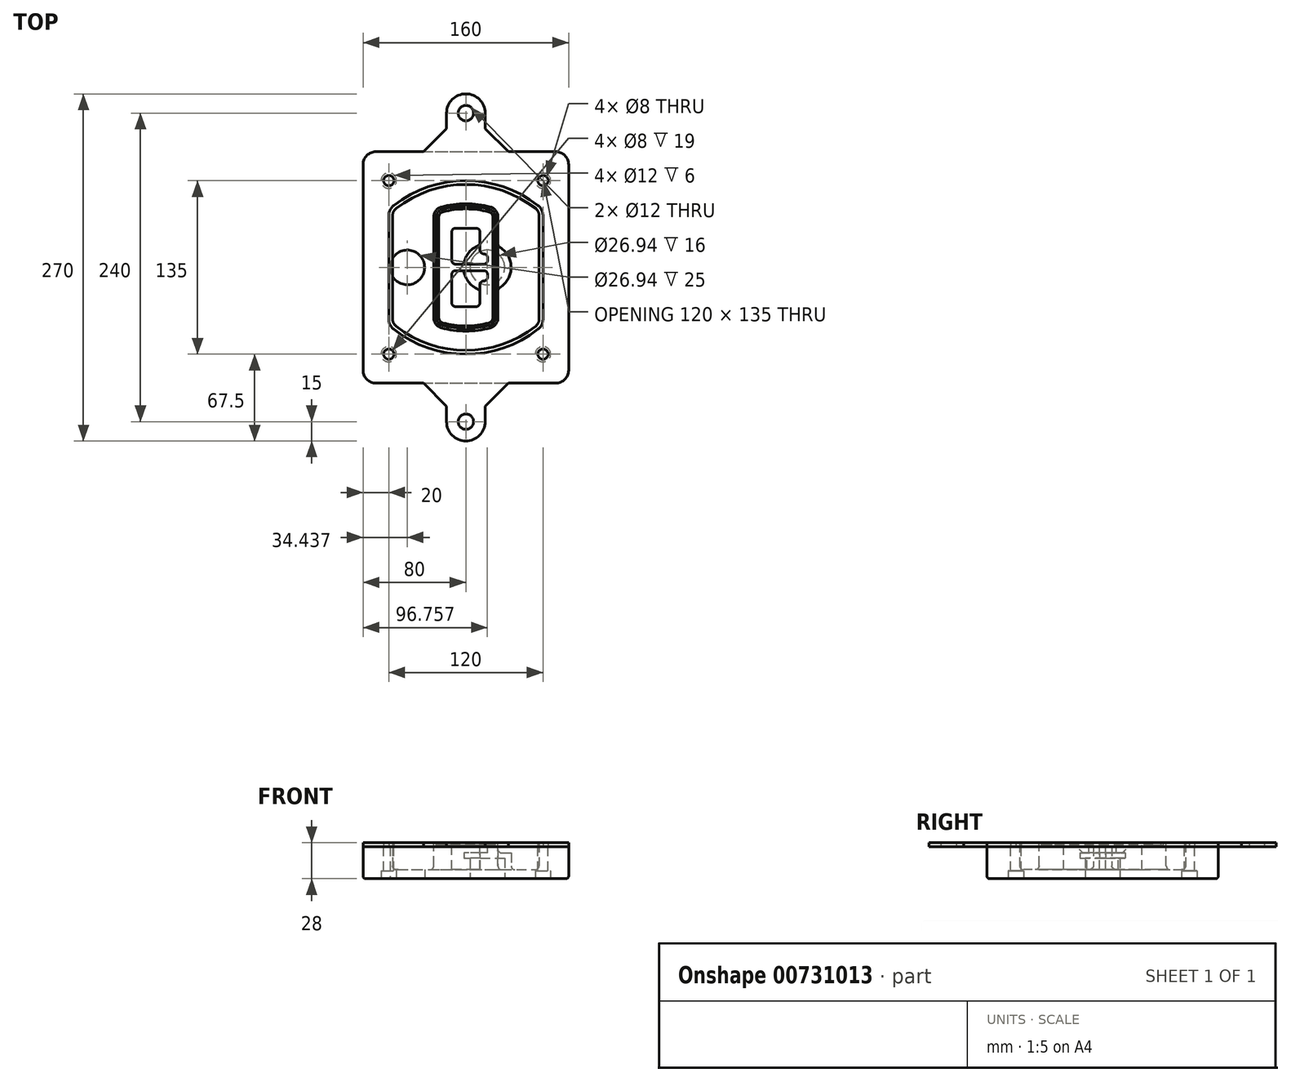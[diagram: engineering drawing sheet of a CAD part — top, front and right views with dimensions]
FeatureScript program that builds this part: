
annotation { "Feature Type Name" : "Feature", "Feature Type Description" : "" }
export const myFeature = defineFeature(function(context is Context, id is Id, definition is map)
    precondition{}
    {
        {
            var Q0;
            Q0=qCreatedBy(makeId("Top.planeOp"),FACE);
            var sketch = newSketch(context, id + "F0", { "sketchPlane" : qUnion([Q0])});
            skPoint(sketch, "E0.rect.middle", {"position": v(0, 0) * mm});
            skLineSegment(sketch, "E1.bottom", {"start": v(-70, -90) * mm, "end": v(70, -90) * mm});
            skLineSegment(sketch, "E1.top", {"start": v(-70, 90) * mm, "end": v(70, 90) * mm});
            skLineSegment(sketch, "E1.left", {"start": v(-80, -80) * mm, "end": v(-80, 80) * mm});
            skLineSegment(sketch, "E1.right", {"start": v(80, -80) * mm, "end": v(80, 80) * mm});
            skLineSegment(sketch, "E2", {"start": v(-80, 90) * mm, "end": v(80, -90) * mm, "construction": true});
            skLineSegment(sketch, "E3", {"start": v(80, 90) * mm, "end": v(-80, -90) * mm, "construction": true});
            skCircle(sketch, "E4", {"center": v(-60, 67.5) * mm, "radius": 4 * mm});
            skCircle(sketch, "E5", {"center": v(60, 67.5) * mm, "radius": 4 * mm});
            skCircle(sketch, "E6", {"center": v(60, -67.5) * mm, "radius": 4 * mm});
            skCircle(sketch, "E7", {"center": v(-60, -67.5) * mm, "radius": 4 * mm});
            skLineSegment(sketch, "E8", {"start": v(-60, 67.5) * mm, "end": v(60, 67.5) * mm, "construction": true});
            skLineSegment(sketch, "E9", {"start": v(60, 67.5) * mm, "end": v(60, -67.5) * mm, "construction": true});
            skLineSegment(sketch, "E10", {"start": v(60, -67.5) * mm, "end": v(-60, -67.5) * mm, "construction": true});
            skLineSegment(sketch, "E11", {"start": v(-60, -67.5) * mm, "end": v(-60, 67.5) * mm, "construction": true});
            skLineSegment(sketch, "E12", {"start": v(-60, 40.3) * mm, "end": v(-60, -40.3) * mm});
            skLineSegment(sketch, "E13", {"start": v(60, 40.3) * mm, "end": v(60, -40.3) * mm});
            skArc(sketch, "E14", {"start": v(56.15, 48.18) * mm, "mid": v(0, 67.5) * mm, "end": v(-56.15, 48.18) * mm});
            skArc(sketch, "E15", {"start": v(-56.15, -48.18) * mm, "mid": v(0, -67.5) * mm, "end": v(56.15, -48.18) * mm});
            skLineSegment(sketch, "E16", {"start": v(-60, 0) * mm, "end": v(60, 0) * mm, "construction": true});
            skPoint(sketch, "E17.visualSharp", {"position": v(-60, -45) * mm});
            skArc(sketch, "E17.filletArc", {"start": v(-60, -40.3) * mm, "mid": v(-58.99, -44.68) * mm, "end": v(-56.15, -48.18) * mm});
            skPoint(sketch, "E18.visualSharp", {"position": v(-60, 45) * mm});
            skArc(sketch, "E18.filletArc", {"start": v(-56.15, 48.18) * mm, "mid": v(-58.99, 44.68) * mm, "end": v(-60, 40.3) * mm});
            skPoint(sketch, "E19.visualSharp", {"position": v(60, 45) * mm});
            skArc(sketch, "E19.filletArc", {"start": v(60, 40.3) * mm, "mid": v(58.99, 44.68) * mm, "end": v(56.15, 48.18) * mm});
            skPoint(sketch, "E20.visualSharp", {"position": v(60, -45) * mm});
            skArc(sketch, "E20.filletArc", {"start": v(56.15, -48.18) * mm, "mid": v(58.99, -44.68) * mm, "end": v(60, -40.3) * mm});
            skPoint(sketch, "E21.visualSharp", {"position": v(-80, 90) * mm});
            skArc(sketch, "E21.filletArc", {"start": v(-70, 90) * mm, "mid": v(-77.07, 87.07) * mm, "end": v(-80, 80) * mm});
            skPoint(sketch, "E22.visualSharp", {"position": v(80, 90) * mm});
            skArc(sketch, "E22.filletArc", {"start": v(80, 80) * mm, "mid": v(77.07, 87.07) * mm, "end": v(70, 90) * mm});
            skPoint(sketch, "E23.visualSharp", {"position": v(80, -90) * mm});
            skArc(sketch, "E23.filletArc", {"start": v(70, -90) * mm, "mid": v(77.07, -87.07) * mm, "end": v(80, -80) * mm});
            skPoint(sketch, "E24.visualSharp", {"position": v(-80, -90) * mm});
            skArc(sketch, "E24.filletArc", {"start": v(-80, -80) * mm, "mid": v(-77.07, -87.07) * mm, "end": v(-70, -90) * mm});
            skArc(sketch, "E25.0", {"start": v(57, 40.3) * mm, "mid": v(56.3, 43.36) * mm, "end": v(54.3, 45.81) * mm});
            skLineSegment(sketch, "E25.1", {"start": v(57, 40.3) * mm, "end": v(57, -40.3) * mm});
            skArc(sketch, "E25.2", {"start": v(54.3, -45.81) * mm, "mid": v(56.3, -43.36) * mm, "end": v(57, -40.3) * mm});
            skArc(sketch, "E25.3", {"start": v(-54.3, -45.81) * mm, "mid": v(0, -64.5) * mm, "end": v(54.3, -45.81) * mm});
            skArc(sketch, "E25.4", {"start": v(-57, -40.3) * mm, "mid": v(-56.3, -43.36) * mm, "end": v(-54.3, -45.81) * mm});
            skArc(sketch, "E25.5", {"start": v(54.3, 45.81) * mm, "mid": v(0, 64.5) * mm, "end": v(-54.3, 45.81) * mm});
            skLineSegment(sketch, "E25.6", {"start": v(-57, 40.3) * mm, "end": v(-57, -40.3) * mm});
            skArc(sketch, "E25.7", {"start": v(-54.3, 45.81) * mm, "mid": v(-56.3, 43.36) * mm, "end": v(-57, 40.3) * mm});
            skArc(sketch, "E26.0", {"start": v(-58.62, 51.33) * mm, "mid": v(-62.58, 46.43) * mm, "end": v(-64, 40.3) * mm});
            skArc(sketch, "E26.1", {"start": v(58.62, 51.33) * mm, "mid": v(0, 71.5) * mm, "end": v(-58.62, 51.33) * mm});
            skArc(sketch, "E26.2", {"start": v(64, 40.3) * mm, "mid": v(62.58, 46.43) * mm, "end": v(58.62, 51.33) * mm});
            skLineSegment(sketch, "E26.3", {"start": v(64, 40.3) * mm, "end": v(64, -40.3) * mm});
            skArc(sketch, "E26.4", {"start": v(58.62, -51.33) * mm, "mid": v(62.58, -46.43) * mm, "end": v(64, -40.3) * mm});
            skLineSegment(sketch, "E26.5", {"start": v(-64, 40.3) * mm, "end": v(-64, -40.3) * mm});
            skArc(sketch, "E26.6", {"start": v(-58.62, -51.33) * mm, "mid": v(0, -71.5) * mm, "end": v(58.62, -51.33) * mm});
            skArc(sketch, "E26.7", {"start": v(-64, -40.3) * mm, "mid": v(-62.58, -46.43) * mm, "end": v(-58.62, -51.33) * mm});
            skSolve(sketch);
        }
        {
            var Q0;
            Q0=makeQuery(id+"F0.imprint","IMPRINT",FACE,{"disambiguationData":[TD([[makeQuery(id+"F0.imprint","IMPRINT",EDGE,{"derivedFrom":sQuery(id+"F0.wireOp",EDGE,"E1.bottom")}),1.0]])]});
            var Q1;
            Q1=makeQuery(id+"F0.imprint","IMPRINT",FACE,{"disambiguationData":[TD([[makeQuery(id+"F0.imprint","IMPRINT",EDGE,{"derivedFrom":sQuery(id+"F0.wireOp",EDGE,"E12")}),1.0]])]});
            var Q2;
            Q2=makeQuery(id+"F0.imprint","IMPRINT",FACE,{"disambiguationData":[TD([[makeQuery(id+"F0.imprint","IMPRINT",EDGE,{"derivedFrom":sQuery(id+"F0.wireOp",EDGE,"E25.0")}),1.0]])]});
            var Q3;
            Q3=makeQuery(id+"F0.imprint","IMPRINT",FACE,{"disambiguationData":[TD([[makeQuery(id+"F0.imprint","IMPRINT",EDGE,{"derivedFrom":sQuery(id+"F0.wireOp",EDGE,"E12")}),-1.0]])]});
            extrude(context, id + "F1", {"entities" : qUnion([Q0, Q1, Q2, Q3]), "oppositeDirection" : true, "depth" : 25 * mm, "offsetDistance" : 25 * mm});
        }
        {
            var Q0;
            Q0=makeQuery(id+"F0.imprint","IMPRINT",FACE,{"disambiguationData":[TD([[makeQuery(id+"F0.imprint","IMPRINT",EDGE,{"derivedFrom":sQuery(id+"F0.wireOp",EDGE,"E12")}),1.0]])]});
            extrude(context, id + "F2", {"entities" : qUnion([Q0]), "operationType" : NewBodyOperationType.ADD, "depth" : 3 * mm, "offsetDistance" : 25 * mm});
        }
        {
            var Q0;
            Q0=makeQuery(id+"F0.imprint","IMPRINT",FACE,{"disambiguationData":[TD([[makeQuery(id+"F0.imprint","IMPRINT",EDGE,{"derivedFrom":sQuery(id+"F0.wireOp",EDGE,"E25.0")}),1.0]])]});
            extrude(context, id + "F3", {"entities" : qUnion([Q0]), "operationType" : NewBodyOperationType.REMOVE, "oppositeDirection" : true, "depth" : 18 * mm, "offsetDistance" : 25 * mm});
        }
        {
            var Q0;
            Q0=makeQuery(id+"F2.opExtrude","CAP_FACE",FACE,{"disambiguationData":[OSD([sQuery(id+"F0.wireOp",EDGE,"E12"),sQuery(id+"F0.wireOp",EDGE,"E13"),sQuery(id+"F0.wireOp",EDGE,"E14"),sQuery(id+"F0.wireOp",EDGE,"E15"),sQuery(id+"F0.wireOp",EDGE,"E17.filletArc"),sQuery(id+"F0.wireOp",EDGE,"E18.filletArc"),sQuery(id+"F0.wireOp",EDGE,"E19.filletArc"),sQuery(id+"F0.wireOp",EDGE,"E20.filletArc"),sQuery(id+"F0.wireOp",EDGE,"E25.0"),sQuery(id+"F0.wireOp",EDGE,"E25.1"),sQuery(id+"F0.wireOp",EDGE,"E25.2"),sQuery(id+"F0.wireOp",EDGE,"E25.3"),sQuery(id+"F0.wireOp",EDGE,"E25.4"),sQuery(id+"F0.wireOp",EDGE,"E25.5"),sQuery(id+"F0.wireOp",EDGE,"E25.6"),sQuery(id+"F0.wireOp",EDGE,"E25.7")])],"isStart":false});
            var sketch = newSketch(context, id + "F4", { "sketchPlane" : qUnion([Q0])});
            skArc(sketch, "E27.0", {"start": v(-19.08, -46.97) * mm, "mid": v(0, -49.5) * mm, "end": v(19.08, -46.97) * mm});
            skArc(sketch, "E28.0", {"start": v(19.08, 46.97) * mm, "mid": v(0, 49.5) * mm, "end": v(-19.08, 46.97) * mm});
            skLineSegment(sketch, "E29", {"start": v(-25, 39.25) * mm, "end": v(-25, -39.25) * mm});
            skLineSegment(sketch, "E30", {"start": v(25, 39.25) * mm, "end": v(25, -39.25) * mm});
            skLineSegment(sketch, "E31", {"start": v(-25, 45.1) * mm, "end": v(25, 45.1) * mm, "construction": true});
            skLineSegment(sketch, "E32", {"start": v(-25, -45.1) * mm, "end": v(25, -45.1) * mm, "construction": true});
            skPoint(sketch, "E33.visualSharp", {"position": v(-25, 45.1) * mm});
            skArc(sketch, "E33.filletArc", {"start": v(-19.08, 46.97) * mm, "mid": v(-23.35, 44.11) * mm, "end": v(-25, 39.25) * mm});
            skPoint(sketch, "E34.visualSharp", {"position": v(25, 45.1) * mm});
            skArc(sketch, "E34.filletArc", {"start": v(25, 39.25) * mm, "mid": v(23.35, 44.11) * mm, "end": v(19.08, 46.97) * mm});
            skPoint(sketch, "E35.visualSharp", {"position": v(25, -45.1) * mm});
            skArc(sketch, "E35.filletArc", {"start": v(19.08, -46.97) * mm, "mid": v(23.35, -44.11) * mm, "end": v(25, -39.25) * mm});
            skPoint(sketch, "E36.visualSharp", {"position": v(-25, -45.1) * mm});
            skArc(sketch, "E36.filletArc", {"start": v(-25, -39.25) * mm, "mid": v(-23.35, -44.11) * mm, "end": v(-19.08, -46.97) * mm});
            skArc(sketch, "E37.0", {"start": v(54.3, 45.81) * mm, "mid": v(0, 64.5) * mm, "end": v(-54.3, 45.81) * mm});
            skArc(sketch, "E37.1", {"start": v(-54.3, 45.81) * mm, "mid": v(-56.3, 43.36) * mm, "end": v(-57, 40.3) * mm});
            skLineSegment(sketch, "E37.2", {"start": v(-57, 40.3) * mm, "end": v(-57, -40.3) * mm});
            skArc(sketch, "E37.3", {"start": v(-57, -40.3) * mm, "mid": v(-56.3, -43.36) * mm, "end": v(-54.3, -45.81) * mm});
            skArc(sketch, "E37.4", {"start": v(-54.3, -45.81) * mm, "mid": v(0, -64.5) * mm, "end": v(54.3, -45.81) * mm});
            skArc(sketch, "E37.5", {"start": v(54.3, -45.81) * mm, "mid": v(56.3, -43.36) * mm, "end": v(57, -40.3) * mm});
            skLineSegment(sketch, "E37.6", {"start": v(57, 40.3) * mm, "end": v(57, -40.3) * mm});
            skArc(sketch, "E37.7", {"start": v(57, 40.3) * mm, "mid": v(56.3, 43.36) * mm, "end": v(54.3, 45.81) * mm});
            skLineSegment(sketch, "E38.0", {"start": v(23, 39.25) * mm, "end": v(23, -39.25) * mm});
            skArc(sketch, "E38.1", {"start": v(18.56, -45.04) * mm, "mid": v(21.76, -42.9) * mm, "end": v(23, -39.25) * mm});
            skArc(sketch, "E38.2", {"start": v(-18.56, -45.04) * mm, "mid": v(0, -47.5) * mm, "end": v(18.56, -45.04) * mm});
            skArc(sketch, "E38.3", {"start": v(-23, -39.25) * mm, "mid": v(-21.76, -42.9) * mm, "end": v(-18.56, -45.04) * mm});
            skLineSegment(sketch, "E38.4", {"start": v(-23, 39.25) * mm, "end": v(-23, -39.25) * mm});
            skArc(sketch, "E38.5", {"start": v(23, 39.25) * mm, "mid": v(21.76, 42.9) * mm, "end": v(18.56, 45.04) * mm});
            skArc(sketch, "E38.6", {"start": v(-18.56, 45.04) * mm, "mid": v(-21.76, 42.9) * mm, "end": v(-23, 39.25) * mm});
            skArc(sketch, "E38.7", {"start": v(18.56, 45.04) * mm, "mid": v(0, 47.5) * mm, "end": v(-18.56, 45.04) * mm});
            skArc(sketch, "E39.0", {"start": v(21, 39.25) * mm, "mid": v(20.18, 41.68) * mm, "end": v(18.04, 43.1) * mm});
            skLineSegment(sketch, "E39.1", {"start": v(21, 39.25) * mm, "end": v(21, -39.25) * mm});
            skArc(sketch, "E39.2", {"start": v(18.04, -43.1) * mm, "mid": v(20.18, -41.68) * mm, "end": v(21, -39.25) * mm});
            skArc(sketch, "E39.3", {"start": v(-18.04, -43.1) * mm, "mid": v(0, -45.5) * mm, "end": v(18.04, -43.1) * mm});
            skArc(sketch, "E39.4", {"start": v(-21, -39.25) * mm, "mid": v(-20.18, -41.68) * mm, "end": v(-18.04, -43.1) * mm});
            skArc(sketch, "E39.5", {"start": v(18.04, 43.1) * mm, "mid": v(0, 45.5) * mm, "end": v(-18.04, 43.1) * mm});
            skLineSegment(sketch, "E39.6", {"start": v(-21, 39.25) * mm, "end": v(-21, -39.25) * mm});
            skArc(sketch, "E39.7", {"start": v(-18.04, 43.1) * mm, "mid": v(-20.18, 41.68) * mm, "end": v(-21, 39.25) * mm});
            skLineSegment(sketch, "E40", {"start": v(-25, 0) * mm, "end": v(25, 0) * mm, "construction": true});
            skLineSegment(sketch, "E41", {"start": v(-11, 5.5) * mm, "end": v(-11, 27.5) * mm});
            skLineSegment(sketch, "E42", {"start": v(-8, 30.5) * mm, "end": v(8, 30.5) * mm});
            skLineSegment(sketch, "E43", {"start": v(11, 27.5) * mm, "end": v(11, 13.5) * mm});
            skLineSegment(sketch, "E44", {"start": v(14, 10.5) * mm, "end": v(14, 10.5) * mm});
            skLineSegment(sketch, "E45", {"start": v(17, 7.5) * mm, "end": v(17, 5.5) * mm});
            skLineSegment(sketch, "E46", {"start": v(14, 2.5) * mm, "end": v(-8, 2.5) * mm});
            skPoint(sketch, "E47.visualSharp", {"position": v(-11, 30.5) * mm});
            skArc(sketch, "E47.filletArc", {"start": v(-8, 30.5) * mm, "mid": v(-10.12, 29.62) * mm, "end": v(-11, 27.5) * mm});
            skPoint(sketch, "E48.visualSharp", {"position": v(11, 30.5) * mm});
            skArc(sketch, "E48.filletArc", {"start": v(11, 27.5) * mm, "mid": v(10.12, 29.62) * mm, "end": v(8, 30.5) * mm});
            skPoint(sketch, "E49.visualSharp", {"position": v(11, 10.5) * mm});
            skArc(sketch, "E49.filletArc", {"start": v(11, 13.5) * mm, "mid": v(11.88, 11.38) * mm, "end": v(14, 10.5) * mm});
            skPoint(sketch, "E50.visualSharp", {"position": v(17, 10.5) * mm});
            skArc(sketch, "E50.filletArc", {"start": v(17, 7.5) * mm, "mid": v(16.12, 9.62) * mm, "end": v(14, 10.5) * mm});
            skPoint(sketch, "E51.visualSharp", {"position": v(17, 2.5) * mm});
            skArc(sketch, "E51.filletArc", {"start": v(14, 2.5) * mm, "mid": v(16.12, 3.38) * mm, "end": v(17, 5.5) * mm});
            skPoint(sketch, "E52.visualSharp", {"position": v(-11, 2.5) * mm});
            skArc(sketch, "E52.filletArc", {"start": v(-11, 5.5) * mm, "mid": v(-10.12, 3.38) * mm, "end": v(-8, 2.5) * mm});
            skLineSegment(sketch, "E53.0.MirrorCS", {"start": v(14, -2.5) * mm, "end": v(-8, -2.5) * mm});
            skArc(sketch, "E54.0.MirrorCS", {"start": v(-11, -5.5) * mm, "mid": v(-10.12, -3.38) * mm, "end": v(-8, -2.5) * mm});
            skLineSegment(sketch, "E55.0.MirrorCS", {"start": v(-11, -5.5) * mm, "end": v(-11, -27.5) * mm});
            skArc(sketch, "E56.0.MirrorCS", {"start": v(-8, -30.5) * mm, "mid": v(-10.12, -29.62) * mm, "end": v(-11, -27.5) * mm});
            skLineSegment(sketch, "E57.0.MirrorCS", {"start": v(-8, -30.5) * mm, "end": v(8, -30.5) * mm});
            skArc(sketch, "E58.0.MirrorCS", {"start": v(11, -27.5) * mm, "mid": v(10.12, -29.62) * mm, "end": v(8, -30.5) * mm});
            skLineSegment(sketch, "E59.0.MirrorCS", {"start": v(11, -27.5) * mm, "end": v(11, -13.5) * mm});
            skArc(sketch, "E60.0.MirrorCS", {"start": v(11, -13.5) * mm, "mid": v(11.88, -11.38) * mm, "end": v(14, -10.5) * mm});
            skArc(sketch, "E61.0.MirrorCS", {"start": v(17, -7.5) * mm, "mid": v(16.12, -9.62) * mm, "end": v(14, -10.5) * mm});
            skLineSegment(sketch, "E62.0.MirrorCS", {"start": v(17, -7.5) * mm, "end": v(17, -5.5) * mm});
            skArc(sketch, "E63.0.MirrorCS", {"start": v(14, -2.5) * mm, "mid": v(16.12, -3.38) * mm, "end": v(17, -5.5) * mm});
            skSolve(sketch);
        }
        {
            var Q0;
            Q0=makeQuery(id+"F4.imprint","IMPRINT",FACE,{"disambiguationData":[TD([[makeQuery(id+"F4.imprint","IMPRINT",EDGE,{"derivedFrom":sQuery(id+"F4.wireOp",EDGE,"E27.0")}),1.0]])]});
            var Q1;
            Q1=makeQuery(id+"F4.imprint","IMPRINT",FACE,{"disambiguationData":[TD([[makeQuery(id+"F4.imprint","IMPRINT",EDGE,{"derivedFrom":sQuery(id+"F4.wireOp",EDGE,"E38.0")}),-1.0]])]});
            var Q2;
            Q2=makeQuery(id+"F4.imprint","IMPRINT",FACE,{"disambiguationData":[TD([[makeQuery(id+"F4.imprint","IMPRINT",EDGE,{"derivedFrom":sQuery(id+"F4.wireOp",EDGE,"E39.0")}),1.0]])]});
            extrude(context, id + "F5", {"entities" : qUnion([Q0, Q1, Q2]), "operationType" : NewBodyOperationType.ADD, "endBound" : BoundingType.UP_TO_NEXT, "oppositeDirection" : true, "depth" : 25 * mm, "offsetDistance" : 25 * mm});
        }
        {
            var Q0;
            Q0=makeQuery(id+"F4.imprint","IMPRINT",FACE,{"disambiguationData":[TD([[makeQuery(id+"F4.imprint","IMPRINT",EDGE,{"derivedFrom":sQuery(id+"F4.wireOp",EDGE,"E38.0")}),-1.0]])]});
            extrude(context, id + "F6", {"entities" : qUnion([Q0]), "operationType" : NewBodyOperationType.REMOVE, "oppositeDirection" : true, "depth" : 2 * mm});
        }
        {
            var Q0;
            Q0=makeQuery(id+"F1.opExtrude","CAP_FACE",FACE,{"disambiguationData":[OSD([sQuery(id+"F0.wireOp",EDGE,"E1.bottom"),sQuery(id+"F0.wireOp",EDGE,"E1.top"),sQuery(id+"F0.wireOp",EDGE,"E1.left"),sQuery(id+"F0.wireOp",EDGE,"E1.right"),sQuery(id+"F0.wireOp",EDGE,"E4"),sQuery(id+"F0.wireOp",EDGE,"E5"),sQuery(id+"F0.wireOp",EDGE,"E6"),sQuery(id+"F0.wireOp",EDGE,"E7"),sQuery(id+"F0.wireOp",EDGE,"E21.filletArc"),sQuery(id+"F0.wireOp",EDGE,"E22.filletArc"),sQuery(id+"F0.wireOp",EDGE,"E23.filletArc"),sQuery(id+"F0.wireOp",EDGE,"E24.filletArc")])],"isStart":false});
            var sketch = newSketch(context, id + "F7", { "sketchPlane" : qUnion([Q0])});
            skCircle(sketch, "E64", {"center": v(16.76, 0) * mm, "radius": 13.47 * mm});
            skCircle(sketch, "E65", {"center": v(-45.56, 0) * mm, "radius": 13.47 * mm});
            skLineSegment(sketch, "E66", {"start": v(80, 0) * mm, "end": v(-80, 0) * mm});
            skCircle(sketch, "E67", {"center": v(16.76, 0) * mm, "radius": 18.47 * mm});
            skCircle(sketch, "E68", {"center": v(60, -67.5) * mm, "radius": 6 * mm});
            skCircle(sketch, "E69", {"center": v(-60, -67.5) * mm, "radius": 6 * mm});
            skCircle(sketch, "E70", {"center": v(-60, 67.5) * mm, "radius": 6 * mm});
            skCircle(sketch, "E71", {"center": v(60, 67.5) * mm, "radius": 6 * mm});
            skSolve(sketch);
        }
        {
            var Q0;
            {var subQ1=sQuery(id+"F7.wireOp",EDGE,"E66");var subQ4=sQuery(id+"F7.wireOp",EDGE,"E64");var subQ6=makeQuery(id+"F7.imprint","INTERSECT",VERTEX,{"disambiguationData":[OD(0.0)],"derivedFrom":[subQ4,subQ1]});Q0=makeQuery(id+"F7.imprint","IMPRINT",FACE,{"disambiguationData":[TD([[makeQuery(id+"F7.imprint","IMPRINT",EDGE,{"disambiguationData":[TD([[subQ6,-1.0]])],"derivedFrom":subQ4}),-1.0]])]});}
            var Q1;
            {var subQ0=sQuery(id+"F7.wireOp",EDGE,"E66");var subQ1=sQuery(id+"F7.wireOp",EDGE,"E64");var subQ3=makeQuery(id+"F7.imprint","INTERSECT",VERTEX,{"disambiguationData":[OD(0.0)],"derivedFrom":[subQ1,subQ0]});Q1=makeQuery(id+"F7.imprint","IMPRINT",FACE,{"disambiguationData":[TD([[makeQuery(id+"F7.imprint","IMPRINT",EDGE,{"disambiguationData":[TD([[subQ3,-1.0]])],"derivedFrom":subQ1}),1.0]])]});}
            var Q2;
            {var subQ0=sQuery(id+"F7.wireOp",EDGE,"E66");var subQ1=sQuery(id+"F7.wireOp",EDGE,"E64");var subQ3=makeQuery(id+"F7.imprint","INTERSECT",VERTEX,{"disambiguationData":[OD(0.0)],"derivedFrom":[subQ1,subQ0]});Q2=makeQuery(id+"F7.imprint","IMPRINT",FACE,{"disambiguationData":[TD([[makeQuery(id+"F7.imprint","IMPRINT",EDGE,{"disambiguationData":[TD([[subQ3,1.0]])],"derivedFrom":subQ1}),1.0]])]});}
            var Q3;
            {var subQ1=sQuery(id+"F7.wireOp",EDGE,"E66");var subQ4=sQuery(id+"F7.wireOp",EDGE,"E64");var subQ6=makeQuery(id+"F7.imprint","INTERSECT",VERTEX,{"disambiguationData":[OD(0.0)],"derivedFrom":[subQ4,subQ1]});Q3=makeQuery(id+"F7.imprint","IMPRINT",FACE,{"disambiguationData":[TD([[makeQuery(id+"F7.imprint","IMPRINT",EDGE,{"disambiguationData":[TD([[subQ6,1.0]])],"derivedFrom":subQ4}),-1.0]])]});}
            extrude(context, id + "F8", {"entities" : qUnion([Q0, Q1, Q2, Q3]), "operationType" : NewBodyOperationType.ADD, "oppositeDirection" : true, "depth" : 20 * mm});
        }
        {
            var Q0;
            {var subQ0=sQuery(id+"F7.wireOp",EDGE,"E66");var subQ1=sQuery(id+"F7.wireOp",EDGE,"E64");var subQ3=makeQuery(id+"F7.imprint","INTERSECT",VERTEX,{"disambiguationData":[OD(0.0)],"derivedFrom":[subQ1,subQ0]});Q0=makeQuery(id+"F7.imprint","IMPRINT",FACE,{"disambiguationData":[TD([[makeQuery(id+"F7.imprint","IMPRINT",EDGE,{"disambiguationData":[TD([[subQ3,-1.0]])],"derivedFrom":subQ1}),1.0]])]});}
            var Q1;
            {var subQ0=sQuery(id+"F7.wireOp",EDGE,"E66");var subQ1=sQuery(id+"F7.wireOp",EDGE,"E64");var subQ3=makeQuery(id+"F7.imprint","INTERSECT",VERTEX,{"disambiguationData":[OD(0.0)],"derivedFrom":[subQ1,subQ0]});Q1=makeQuery(id+"F7.imprint","IMPRINT",FACE,{"disambiguationData":[TD([[makeQuery(id+"F7.imprint","IMPRINT",EDGE,{"disambiguationData":[TD([[subQ3,1.0]])],"derivedFrom":subQ1}),1.0]])]});}
            extrude(context, id + "F9", {"entities" : qUnion([Q0, Q1]), "operationType" : NewBodyOperationType.REMOVE, "oppositeDirection" : true, "depth" : 16 * mm});
        }
        {
            var Q0;
            {var subQ0=sQuery(id+"F7.wireOp",EDGE,"E66");var subQ1=sQuery(id+"F7.wireOp",EDGE,"E65");var subQ3=makeQuery(id+"F7.imprint","INTERSECT",VERTEX,{"disambiguationData":[OD(0.0)],"derivedFrom":[subQ1,subQ0]});Q0=makeQuery(id+"F7.imprint","IMPRINT",FACE,{"disambiguationData":[TD([[makeQuery(id+"F7.imprint","IMPRINT",EDGE,{"disambiguationData":[TD([[subQ3,-1.0]])],"derivedFrom":subQ1}),1.0]])]});}
            var Q1;
            {var subQ0=sQuery(id+"F7.wireOp",EDGE,"E66");var subQ1=sQuery(id+"F7.wireOp",EDGE,"E65");var subQ3=makeQuery(id+"F7.imprint","INTERSECT",VERTEX,{"disambiguationData":[OD(0.0)],"derivedFrom":[subQ1,subQ0]});Q1=makeQuery(id+"F7.imprint","IMPRINT",FACE,{"disambiguationData":[TD([[makeQuery(id+"F7.imprint","IMPRINT",EDGE,{"disambiguationData":[TD([[subQ3,1.0]])],"derivedFrom":subQ1}),1.0]])]});}
            extrude(context, id + "F10", {"entities" : qUnion([Q0, Q1]), "operationType" : NewBodyOperationType.REMOVE, "oppositeDirection" : true, "depth" : 25 * mm});
        }
        {
            var Q0;
            Q0=makeQuery(id+"F7.imprint","IMPRINT",FACE,{"disambiguationData":[TD([[makeQuery(id+"F7.imprint","IMPRINT",EDGE,{"derivedFrom":sQuery(id+"F7.wireOp",EDGE,"E68")}),1.0]])]});
            var Q1;
            Q1=makeQuery(id+"F7.imprint","IMPRINT",FACE,{"disambiguationData":[TD([[makeQuery(id+"F7.imprint","IMPRINT",EDGE,{"derivedFrom":makeQuery(id+"F1.opExtrude","CAP_EDGE",EDGE,{"disambiguationData":[OSD([sQuery(id+"F0.wireOp",EDGE,"E5")])],"isStart":false})}),-1.0]])]});
            var Q2;
            Q2=makeQuery(id+"F7.imprint","IMPRINT",FACE,{"disambiguationData":[TD([[makeQuery(id+"F7.imprint","IMPRINT",EDGE,{"derivedFrom":sQuery(id+"F7.wireOp",EDGE,"E69")}),1.0]])]});
            var Q3;
            Q3=makeQuery(id+"F7.imprint","IMPRINT",FACE,{"disambiguationData":[TD([[makeQuery(id+"F7.imprint","IMPRINT",EDGE,{"derivedFrom":makeQuery(id+"F1.opExtrude","CAP_EDGE",EDGE,{"disambiguationData":[OSD([sQuery(id+"F0.wireOp",EDGE,"E4")])],"isStart":false})}),-1.0]])]});
            var Q4;
            Q4=makeQuery(id+"F7.imprint","IMPRINT",FACE,{"disambiguationData":[TD([[makeQuery(id+"F7.imprint","IMPRINT",EDGE,{"derivedFrom":sQuery(id+"F7.wireOp",EDGE,"E70")}),1.0]])]});
            var Q5;
            Q5=makeQuery(id+"F7.imprint","IMPRINT",FACE,{"disambiguationData":[TD([[makeQuery(id+"F7.imprint","IMPRINT",EDGE,{"derivedFrom":makeQuery(id+"F1.opExtrude","CAP_EDGE",EDGE,{"disambiguationData":[OSD([sQuery(id+"F0.wireOp",EDGE,"E7")])],"isStart":false})}),-1.0]])]});
            var Q6;
            Q6=makeQuery(id+"F7.imprint","IMPRINT",FACE,{"disambiguationData":[TD([[makeQuery(id+"F7.imprint","IMPRINT",EDGE,{"derivedFrom":sQuery(id+"F7.wireOp",EDGE,"E71")}),1.0]])]});
            var Q7;
            Q7=makeQuery(id+"F7.imprint","IMPRINT",FACE,{"disambiguationData":[TD([[makeQuery(id+"F7.imprint","IMPRINT",EDGE,{"derivedFrom":makeQuery(id+"F1.opExtrude","CAP_EDGE",EDGE,{"disambiguationData":[OSD([sQuery(id+"F0.wireOp",EDGE,"E6")])],"isStart":false})}),-1.0]])]});
            extrude(context, id + "F11", {"entities" : qUnion([Q0, Q1, Q2, Q3, Q4, Q5, Q6, Q7]), "operationType" : NewBodyOperationType.REMOVE, "oppositeDirection" : true, "depth" : 6 * mm});
        }
        {
            var Q0;
            Q0=makeQuery(id+"F9.boolean.opBoolean","COPY",FACE,{"derivedFrom":makeQuery(id+"F9.opExtrude","CAP_FACE",FACE,{"disambiguationData":[OSD([sQuery(id+"F7.wireOp",EDGE,"E64")])],"isStart":false})});
            var sketch = newSketch(context, id + "F12", { "sketchPlane" : qUnion([Q0])});
            skArc(sketch, "E72.0", {"start": v(11, 17.55) * mm, "mid": v(2.57, 11.82) * mm, "end": v(-1.54, 2.5) * mm});
            skArc(sketch, "E72.1", {"start": v(-1.54, -2.5) * mm, "mid": v(2.57, -11.82) * mm, "end": v(11, -17.55) * mm});
            skLineSegment(sketch, "E73", {"start": v(-1.54, -2.5) * mm, "end": v(14, -2.5) * mm});
            skLineSegment(sketch, "E74.0", {"start": v(14, 2.5) * mm, "end": v(-1.54, 2.5) * mm});
            skArc(sketch, "E74.1", {"start": v(14, 2.5) * mm, "mid": v(16.12, 3.38) * mm, "end": v(17, 5.5) * mm});
            skLineSegment(sketch, "E74.2", {"start": v(17, 7.5) * mm, "end": v(17, 5.5) * mm});
            skArc(sketch, "E74.3", {"start": v(17, 7.5) * mm, "mid": v(16.12, 9.62) * mm, "end": v(14, 10.5) * mm});
            skArc(sketch, "E74.4", {"start": v(11, 13.5) * mm, "mid": v(11.88, 11.38) * mm, "end": v(14, 10.5) * mm});
            skLineSegment(sketch, "E74.5", {"start": v(11, 17.55) * mm, "end": v(11, 13.5) * mm});
            skLineSegment(sketch, "E74.7", {"start": v(14, -2.5) * mm, "end": v(-1.54, -2.5) * mm});
            skArc(sketch, "E74.8", {"start": v(14, -2.5) * mm, "mid": v(16.12, -3.38) * mm, "end": v(17, -5.5) * mm});
            skLineSegment(sketch, "E74.9", {"start": v(17, -7.5) * mm, "end": v(17, -5.5) * mm});
            skArc(sketch, "E74.10", {"start": v(17, -7.5) * mm, "mid": v(16.12, -9.62) * mm, "end": v(14, -10.5) * mm});
            skArc(sketch, "E74.11", {"start": v(11, -13.5) * mm, "mid": v(11.88, -11.38) * mm, "end": v(14, -10.5) * mm});
            skLineSegment(sketch, "E74.12", {"start": v(11, -17.55) * mm, "end": v(11, -13.5) * mm});
            skPoint(sketch, "E75.orphan", {"position": v(11, -27.5) * mm});
            skPoint(sketch, "E76.orphan", {"position": v(-8, -2.5) * mm});
            skPoint(sketch, "E77.orphan", {"position": v(-8, 2.5) * mm});
            skPoint(sketch, "E78.orphan", {"position": v(11, 27.5) * mm});
            skSolve(sketch);
        }
        {
            var Q0;
            {var subQ7=sQuery(id+"F12.wireOp",EDGE,"E72.0");var subQ14=sQuery(id+"F12.wireOp",EDGE,"E72.1");var subQ16=sQuery(id+"F12.wireOp",EDGE,"E74.1");var subQ18=sQuery(id+"F12.wireOp",EDGE,"E74.8");Q0=qUnion([makeQuery(id+"F12.imprint","IMPRINT",FACE,{"disambiguationData":[TD([[makeQuery(id+"F12.imprint","IMPRINT",EDGE,{"derivedFrom":subQ7}),1.0]])]}),makeQuery(id+"F12.imprint","IMPRINT",FACE,{"disambiguationData":[TD([[makeQuery(id+"F12.imprint","IMPRINT",EDGE,{"derivedFrom":subQ14}),1.0]])]}),makeQuery(id+"F12.imprint","IMPRINT",FACE,{"disambiguationData":[TD([[makeQuery(id+"F12.imprint","IMPRINT",EDGE,{"derivedFrom":subQ16}),1.0]])]}),makeQuery(id+"F12.imprint","IMPRINT",FACE,{"disambiguationData":[TD([[makeQuery(id+"F12.imprint","IMPRINT",EDGE,{"derivedFrom":subQ18}),-1.0]])]})]);}
            var Q1;
            Q1=makeQuery(id+"F5.boolean.opBoolean","SPLIT",FACE,{"disambiguationData":[TD([makeQuery(id+"F5.opExtrude","SWEPT_FACE",FACE,{"disambiguationData":[OSD([sQuery(id+"F4.wireOp",EDGE,"E41")])]})])],"derivedFrom":makeQuery(id+"F3.boolean.opBoolean","COPY",FACE,{"derivedFrom":makeQuery(id+"F3.opExtrude","CAP_FACE",FACE,{"disambiguationData":[OSD([sQuery(id+"F0.wireOp",EDGE,"E25.0"),sQuery(id+"F0.wireOp",EDGE,"E25.1"),sQuery(id+"F0.wireOp",EDGE,"E25.2"),sQuery(id+"F0.wireOp",EDGE,"E25.3"),sQuery(id+"F0.wireOp",EDGE,"E25.4"),sQuery(id+"F0.wireOp",EDGE,"E25.5"),sQuery(id+"F0.wireOp",EDGE,"E25.6"),sQuery(id+"F0.wireOp",EDGE,"E25.7")])],"isStart":false})})});
            extrude(context, id + "F13", {"entities" : qUnion([Q0]), "operationType" : NewBodyOperationType.REMOVE, "endBound" : BoundingType.UP_TO_SURFACE, "endBoundEntityFace" : qUnion([Q1]), "depth" : 25 * mm});
        }
        {
            var Q0;
            Q0=makeQuery(id+"F3.boolean.opBoolean","COPY",EDGE,{"derivedFrom":makeQuery(id+"F3.opExtrude","CAP_EDGE",EDGE,{"disambiguationData":[OSD([sQuery(id+"F0.wireOp",EDGE,"E25.6")])],"isStart":false})});
            var Q1;
            Q1=makeQuery(id+"F8.boolean.opBoolean","INTERSECT",EDGE,{"derivedFrom":[makeQuery(id+"F5.opExtrude","SWEPT_FACE",FACE,{"disambiguationData":[OSD([sQuery(id+"F4.wireOp",EDGE,"E30")])]}),makeQuery(id+"F8.opExtrude","CAP_FACE",FACE,{"disambiguationData":[OSD([sQuery(id+"F7.wireOp",EDGE,"E67")])],"isStart":false})]});
            var Q2;
            Q2=makeQuery(id+"F8.boolean.opBoolean","INTERSECT",EDGE,{"disambiguationData":[OD(1.0)],"derivedFrom":[makeQuery(id+"F5.opExtrude","SWEPT_FACE",FACE,{"disambiguationData":[OSD([sQuery(id+"F4.wireOp",EDGE,"E30")])]}),makeQuery(id+"F8.opExtrude","SWEPT_FACE",FACE,{"disambiguationData":[OSD([sQuery(id+"F7.wireOp",EDGE,"E67")])]})]});
            var Q3;
            {var subQ0=sQuery(id+"F4.wireOp",EDGE,"E30");Q3=makeQuery(id+"F8.boolean.opBoolean","SPLIT",EDGE,{"disambiguationData":[TD([makeQuery(id+"F5.opExtrude","SWEPT_FACE",FACE,{"disambiguationData":[OSD([sQuery(id+"F4.wireOp",EDGE,"E35.filletArc")])]})])],"derivedFrom":makeQuery(id+"F5.opExtrude","CAP_EDGE",EDGE,{"disambiguationData":[OSD([subQ0])],"isStart":false})});}
            var Q4;
            {var subQ0=sQuery(id+"F0.wireOp",EDGE,"E25.7");var subQ1=sQuery(id+"F0.wireOp",EDGE,"E25.1");var subQ2=sQuery(id+"F0.wireOp",EDGE,"E25.6");var subQ3=sQuery(id+"F0.wireOp",EDGE,"E25.5");var subQ4=sQuery(id+"F0.wireOp",EDGE,"E25.4");var subQ5=sQuery(id+"F0.wireOp",EDGE,"E25.0");var subQ6=sQuery(id+"F0.wireOp",EDGE,"E25.2");var subQ7=sQuery(id+"F0.wireOp",EDGE,"E25.3");Q4=makeQuery(id+"F8.boolean.opBoolean","INTERSECT",EDGE,{"derivedFrom":[makeQuery(id+"F5.boolean.opBoolean","SPLIT",FACE,{"disambiguationData":[TD([makeQuery(id+"F2.opExtrude","SWEPT_FACE",FACE,{"disambiguationData":[OSD([subQ5])]})])],"derivedFrom":makeQuery(id+"F3.boolean.opBoolean","COPY",FACE,{"derivedFrom":makeQuery(id+"F3.opExtrude","CAP_FACE",FACE,{"disambiguationData":[OSD([subQ5,subQ1,subQ6,subQ7,subQ4,subQ3,subQ2,subQ0])],"isStart":false})})}),makeQuery(id+"F8.opExtrude","SWEPT_FACE",FACE,{"disambiguationData":[OSD([sQuery(id+"F7.wireOp",EDGE,"E67")])]})]});}
            var Q5;
            Q5=makeQuery(id+"F8.boolean.opBoolean","INTERSECT",EDGE,{"disambiguationData":[OD(0.0)],"derivedFrom":[makeQuery(id+"F5.opExtrude","SWEPT_FACE",FACE,{"disambiguationData":[OSD([sQuery(id+"F4.wireOp",EDGE,"E30")])]}),makeQuery(id+"F8.opExtrude","SWEPT_FACE",FACE,{"disambiguationData":[OSD([sQuery(id+"F7.wireOp",EDGE,"E67")])]})]});
            fillet(context, id + "F14", {"entities" : qUnion([Q0, Q1, Q2, Q3, Q4, Q5]), "radius" : 3 * mm, "tangentPropagation" : true, "allowEdgeOverflow" : false});
        }
        {
            var Q0;
            Q0=makeQuery(id+"F1.opExtrude","CAP_EDGE",EDGE,{"disambiguationData":[OSD([sQuery(id+"F0.wireOp",EDGE,"E1.bottom")])],"isStart":false});
            fillet(context, id + "F15", {"entities" : qUnion([Q0]), "radius" : 2 * mm, "tangentPropagation" : true, "allowEdgeOverflow" : false});
        }
        {
            var Q0;
            {var subQ0=sQuery(id+"F0.wireOp",EDGE,"E21.filletArc");var subQ1=sQuery(id+"F0.wireOp",EDGE,"E7");var subQ2=sQuery(id+"F0.wireOp",EDGE,"E6");var subQ3=sQuery(id+"F0.wireOp",EDGE,"E5");var subQ4=sQuery(id+"F0.wireOp",EDGE,"E4");var subQ5=sQuery(id+"F0.wireOp",EDGE,"E22.filletArc");var subQ6=sQuery(id+"F0.wireOp",EDGE,"E1.bottom");var subQ7=sQuery(id+"F0.wireOp",EDGE,"E1.right");var subQ8=sQuery(id+"F0.wireOp",EDGE,"E1.top");var subQ9=sQuery(id+"F0.wireOp",EDGE,"E1.left");var subQ10=sQuery(id+"F0.wireOp",EDGE,"E23.filletArc");var subQ11=sQuery(id+"F0.wireOp",EDGE,"E24.filletArc");Q0=makeQuery(id+"F2.boolean.opBoolean","SPLIT",FACE,{"disambiguationData":[TD([makeQuery(id+"F1.opExtrude","SWEPT_FACE",FACE,{"disambiguationData":[OSD([subQ6])]})])],"derivedFrom":makeQuery(id+"F1.opExtrude","CAP_FACE",FACE,{"disambiguationData":[OSD([subQ6,subQ8,subQ9,subQ7,subQ4,subQ3,subQ2,subQ1,subQ0,subQ5,subQ10,subQ11])],"isStart":true})});}
            var sketch = newSketch(context, id + "F16", { "sketchPlane" : qUnion([Q0])});
            skLineSegment(sketch, "E79", {"start": v(0, 90) * mm, "end": v(0, 120) * mm, "construction": true});
            skCircle(sketch, "E80", {"center": v(0, 120) * mm, "radius": 6 * mm});
            skArc(sketch, "E81", {"start": v(15, 120) * mm, "mid": v(0, 135) * mm, "end": v(-15, 120) * mm});
            skLineSegment(sketch, "E82", {"start": v(-33, 90) * mm, "end": v(-15, 108) * mm});
            skLineSegment(sketch, "E83", {"start": v(-15, 108) * mm, "end": v(-15, 120) * mm});
            skLineSegment(sketch, "E84", {"start": v(15, 120) * mm, "end": v(15, 108) * mm});
            skLineSegment(sketch, "E85", {"start": v(15, 108) * mm, "end": v(33, 90) * mm});
            skLineSegment(sketch, "E86.0", {"start": v(-70, 90) * mm, "end": v(-33, 90) * mm});
            skArc(sketch, "E87.0", {"start": v(-70, 90) * mm, "mid": v(-77.07, 87.07) * mm, "end": v(-80, 80) * mm});
            skLineSegment(sketch, "E88.0.0", {"start": v(70, 90) * mm, "end": v(33, 90) * mm});
            skLineSegment(sketch, "E88.0.2", {"start": v(-80, 80) * mm, "end": v(-80, -80) * mm});
            skArc(sketch, "E88.0.3", {"start": v(-80, -80) * mm, "mid": v(-77.07, -87.07) * mm, "end": v(-70, -90) * mm});
            skLineSegment(sketch, "E88.0.4", {"start": v(-70, -90) * mm, "end": v(-33, -90) * mm});
            skArc(sketch, "E88.0.5", {"start": v(70, -90) * mm, "mid": v(77.07, -87.07) * mm, "end": v(80, -80) * mm});
            skLineSegment(sketch, "E88.0.6", {"start": v(80, -80) * mm, "end": v(80, 80) * mm});
            skArc(sketch, "E88.0.7", {"start": v(80, 80) * mm, "mid": v(77.07, 87.07) * mm, "end": v(70, 90) * mm});
            skLineSegment(sketch, "E89", {"start": v(-80, 0) * mm, "end": v(80, 0) * mm, "construction": true});
            skLineSegment(sketch, "E90.MirrorCS", {"start": v(15, -108) * mm, "end": v(33, -90) * mm});
            skLineSegment(sketch, "E91.MirrorCS", {"start": v(15, -120) * mm, "end": v(15, -108) * mm});
            skLineSegment(sketch, "E92.MirrorCS", {"start": v(-15, -108) * mm, "end": v(-15, -120) * mm});
            skLineSegment(sketch, "E93.MirrorCS", {"start": v(-33, -90) * mm, "end": v(-15, -108) * mm});
            skArc(sketch, "E94.MirrorCS", {"start": v(15, -120) * mm, "mid": v(0, -135) * mm, "end": v(-15, -120) * mm});
            skCircle(sketch, "E95.MirrorC", {"center": v(0, -120) * mm, "radius": 6 * mm});
            skLineSegment(sketch, "E96.MirrorCS", {"start": v(0, -90) * mm, "end": v(0, -120) * mm, "construction": true});
            skCircle(sketch, "E97.0", {"center": v(-60, 67.5) * mm, "radius": 4 * mm});
            skCircle(sketch, "E98.0", {"center": v(-60, -67.5) * mm, "radius": 4 * mm});
            skCircle(sketch, "E99.0", {"center": v(60, -67.5) * mm, "radius": 4 * mm});
            skCircle(sketch, "E100.0", {"center": v(60, 67.5) * mm, "radius": 4 * mm});
            skLineSegment(sketch, "E101.trimOffspring", {"start": v(-33, 90) * mm, "end": v(-70, 90) * mm});
            skLineSegment(sketch, "E102.trimOffspring", {"start": v(33, -90) * mm, "end": v(70, -90) * mm});
            skLineSegment(sketch, "E103.trimOffspring", {"start": v(33, 90) * mm, "end": v(70, 90) * mm});
            skArc(sketch, "E104.0", {"start": v(-56.15, -48.18) * mm, "mid": v(0, -67.5) * mm, "end": v(56.15, -48.18) * mm});
            skArc(sketch, "E105.0", {"start": v(56.15, -48.18) * mm, "mid": v(58.99, -44.68) * mm, "end": v(60, -40.3) * mm});
            skLineSegment(sketch, "E106.0", {"start": v(60, 40.3) * mm, "end": v(60, -40.3) * mm});
            skPoint(sketch, "E107.0", {"position": v(58.99, 44.68) * mm});
            skArc(sketch, "E108.0", {"start": v(60, 40.3) * mm, "mid": v(58.99, 44.68) * mm, "end": v(56.15, 48.18) * mm});
            skArc(sketch, "E109.0", {"start": v(56.15, 48.18) * mm, "mid": v(0, 67.5) * mm, "end": v(-56.15, 48.18) * mm});
            skArc(sketch, "E110.0", {"start": v(-56.15, 48.18) * mm, "mid": v(-58.99, 44.68) * mm, "end": v(-60, 40.3) * mm});
            skLineSegment(sketch, "E111.0", {"start": v(-60, 40.3) * mm, "end": v(-60, -40.3) * mm});
            skArc(sketch, "E112.0", {"start": v(-60, -40.3) * mm, "mid": v(-58.99, -44.68) * mm, "end": v(-56.15, -48.18) * mm});
            skSolve(sketch);
        }
        {
            var Q0;
            Q0=makeQuery(id+"F16.imprint","IMPRINT",FACE,{"disambiguationData":[TD([[makeQuery(id+"F16.imprint","IMPRINT",EDGE,{"derivedFrom":sQuery(id+"F16.wireOp",EDGE,"E80")}),-1.0]])]});
            var Q1;
            Q1=makeQuery(id+"F16.imprint","IMPRINT",FACE,{"disambiguationData":[TD([[makeQuery(id+"F16.imprint","IMPRINT",EDGE,{"derivedFrom":sQuery(id+"F16.wireOp",EDGE,"E87.0")}),1.0]])]});
            var Q2;
            {var subQ2=sQuery(id+"F16.wireOp",EDGE,"E90.MirrorCS");Q2=makeQuery(id+"F16.imprint","IMPRINT",FACE,{"disambiguationData":[TD([[makeQuery(id+"F16.imprint","IMPRINT",EDGE,{"derivedFrom":subQ2}),1.0]])]});}
            var Q3;
            Q3=makeQuery(id+"F2.opExtrude","CAP_FACE",FACE,{"disambiguationData":[OSD([sQuery(id+"F0.wireOp",EDGE,"E12"),sQuery(id+"F0.wireOp",EDGE,"E13"),sQuery(id+"F0.wireOp",EDGE,"E14"),sQuery(id+"F0.wireOp",EDGE,"E15"),sQuery(id+"F0.wireOp",EDGE,"E17.filletArc"),sQuery(id+"F0.wireOp",EDGE,"E18.filletArc"),sQuery(id+"F0.wireOp",EDGE,"E19.filletArc"),sQuery(id+"F0.wireOp",EDGE,"E20.filletArc"),sQuery(id+"F0.wireOp",EDGE,"E25.0"),sQuery(id+"F0.wireOp",EDGE,"E25.1"),sQuery(id+"F0.wireOp",EDGE,"E25.2"),sQuery(id+"F0.wireOp",EDGE,"E25.3"),sQuery(id+"F0.wireOp",EDGE,"E25.4"),sQuery(id+"F0.wireOp",EDGE,"E25.5"),sQuery(id+"F0.wireOp",EDGE,"E25.6"),sQuery(id+"F0.wireOp",EDGE,"E25.7")])],"isStart":false});
            extrude(context, id + "F17", {"entities" : qUnion([Q0, Q1, Q2]), "endBound" : BoundingType.UP_TO_SURFACE, "depth" : 25 * mm, "endBoundEntityFace" : qUnion([Q3]), "offsetDistance" : 25 * mm});
        }
    });
